# Revit family: Tyco_FireDtctnAlmCtrlIndctEquip_FireClass-OutdoorAddressableCallpoint
name_source: partatom
category: Fire Alarm Devices
revit_build: Autodesk Revit MEP 2013 (Build: 20120221_2030(x64)
units: mm (PartAtom-declared; Revit-internal decimal feet)

## types (1)
- FC421CP-I
    AssetType = Moveable
    BIMObjectName = Tyco_FireDtctnAlmCtrlIndctEquip_FireClass-OutdoorAddressableCallpoint-FC421CP-I
    Brand = FireClass
    Category = Ee_40_15_75
    Color = Red RAL3001
    Component Color = Material Red
    Default Elevation = 1200 mm
    Description = FireClass-Outdoor Weatherproof Resettable Callpoint with Short-Circuit Isolator
    DurationUnit = Year
    Environment = Outdoor applications
    HasProtectiveEarth = No
    IPCode = IP67
    IfcExportAs = IfcDistributionElement
    IfcExportType = NOTDEFINED
    IfcTypeObject = IfcBuildingElementProxy
    Manufacturer = Tyco Fire Protection Products
    ManufacturerName = Tyco Fire Protection Products
    ManufacturerURL = www.fireclass.net
    Material = Flame Retardant ABS
    Model = FC421CP-I
    ModelNumber = FC421CP-I
    NBSDescription = Fire detection and alarm control and indicating equipment (CIE)
    NBSReference = 90-75-30/380
    Name = FC421CP-I Outdoor Weatherproof Resettable Callpoint with Short-Circuit Isolator
    NominalHeight = 93 mm  [stored 0.305118 ft]
    NominalLength = 98 mm
    NominalVoltage = 40 V DC
    NominalWidth = 73 mm  [stored 0.239501 ft]
    NumberOfPoles = 0
    OperationTemperatureRange = -25 °C to +70 °C
    PhaseAngle = 0.00°
    ProductCodes = 514.800.806
    ProductInformation = https://fireclass.co.uk
    ProductSpecification = FC421CP-I Outdoor Weatherproof Resettable Callpoint with Short-Circuit Isolator
    RelativeHumidity = up to 95%  (non- condensing)
    StorageTemperature = -30 °C to +70 °C
    URL = https://fireclass.co.uk
    Uniclass2 = Ee_40_15_75
    UsageCurrent = 300μA
    Version = 1
    WarrantyDurationLabor = 1.5 years
    WarrantyDurationParts = 1.5 years
    WarrantyDurationUnit = Year
    Weight = 240g

note: [stored X ft] marks values corroborated as IEEE doubles in the binary element streams (Revit-internal decimal feet)

## geometry (parser evidence)
native form markers: Sweep x2
no freeform markers — native parametric forms only
